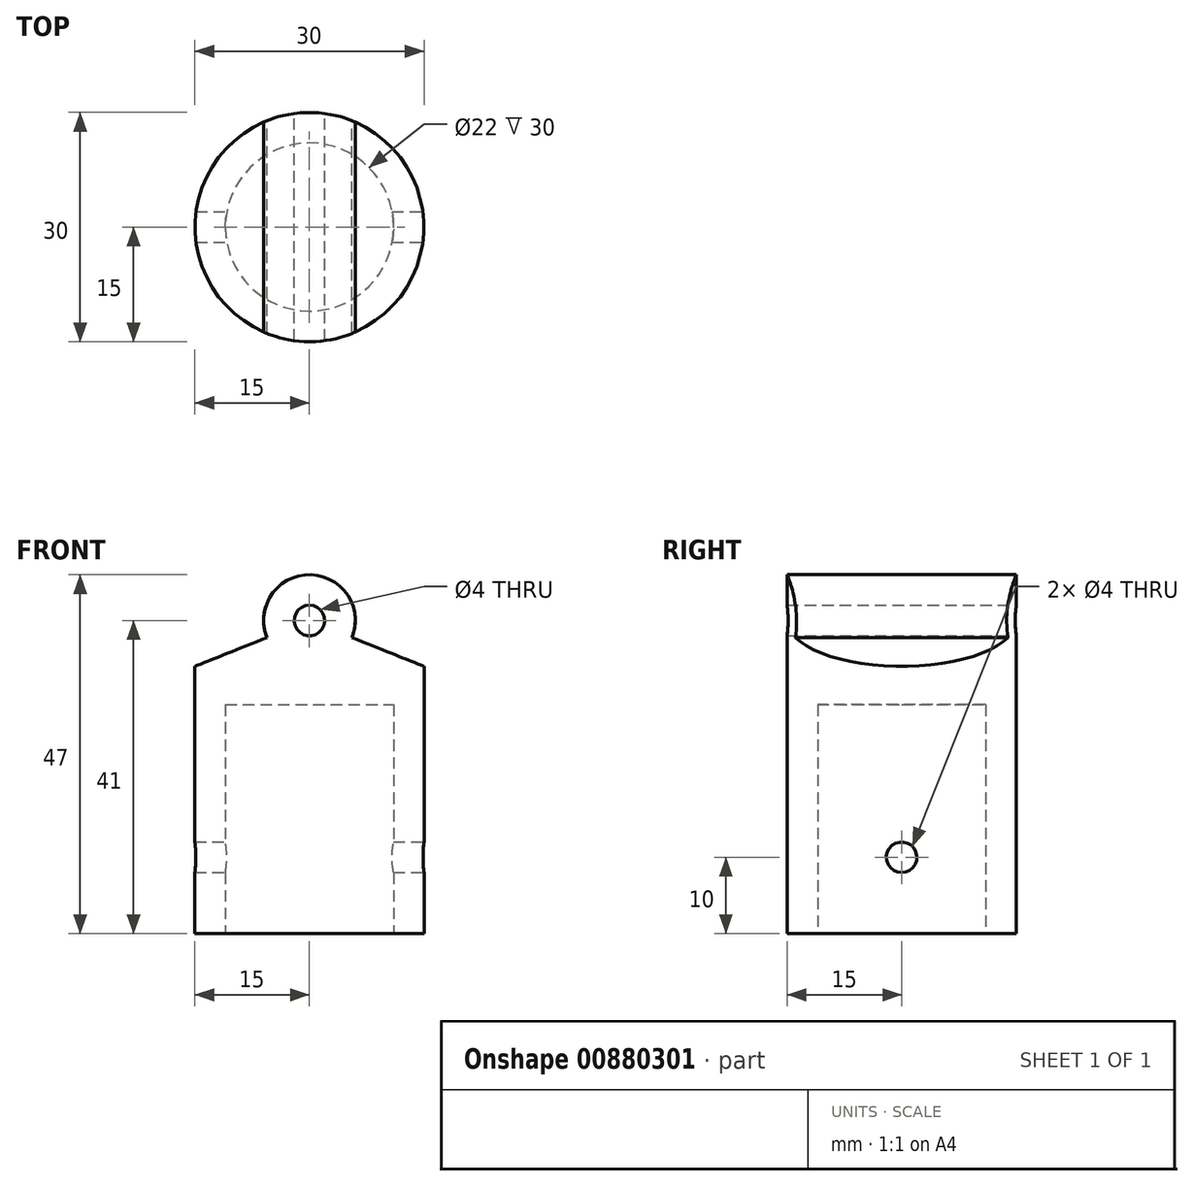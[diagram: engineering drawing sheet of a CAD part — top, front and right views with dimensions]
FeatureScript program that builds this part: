
annotation { "Feature Type Name" : "Feature", "Feature Type Description" : "" }
export const myFeature = defineFeature(function(context is Context, id is Id, definition is map)
    precondition{}
    {
        {
            var Q0;
            Q0=qCreatedBy(makeId("Top.planeOp"),FACE);
            var sketch = newSketch(context, id + "F0", { "sketchPlane" : qUnion([Q0])});
            skCircle(sketch, "E0", {"center": v(0, 0) * mm, "radius": 15 * mm});
            skSolve(sketch);
        }
        {
            var Q0;
            Q0=makeQuery(id+"F0.imprint","IMPRINT",FACE,{"disambiguationData":[TD([[makeQuery(id+"F0.imprint","IMPRINT",EDGE,{"derivedFrom":sQuery(id+"F0.wireOp",EDGE,"E0")}),1.0]])]});
            extrude(context, id + "F1", {"entities" : qUnion([Q0]), "depth" : 35 * mm, "offsetDistance" : 25 * mm});
        }
        {
            var Q0;
            Q0=qCreatedBy(makeId("Front.planeOp"),FACE);
            var sketch = newSketch(context, id + "F2", { "sketchPlane" : qUnion([Q0])});
            skCircle(sketch, "E1", {"center": v(0, 41) * mm, "radius": 6 * mm});
            skCircle(sketch, "E2", {"center": v(0, 41) * mm, "radius": 2 * mm});
            skLineSegment(sketch, "E3", {"start": v(-15, 35) * mm, "end": v(15, 35) * mm});
            skLineSegment(sketch, "E4", {"start": v(-15, 35) * mm, "end": v(0, 41) * mm});
            skLineSegment(sketch, "E5", {"start": v(15, 35) * mm, "end": v(0, 41) * mm});
            skSolve(sketch);
        }
        {
            var Q0;
            {var subQ0=sQuery(id+"F2.wireOp",EDGE,"E3");var subQ1=sQuery(id+"F2.wireOp",EDGE,"E1");var subQ2=makeQuery(id+"F2.imprint","INTERSECT",VERTEX,{"derivedFrom":[subQ1,subQ0]});Q0=makeQuery(id+"F2.imprint","IMPRINT",FACE,{"disambiguationData":[TD([[makeQuery(id+"F2.imprint","IMPRINT",EDGE,{"disambiguationData":[TD([[subQ2,1.0]])],"derivedFrom":subQ1}),-1.0]])]});}
            var Q1;
            {var subQ1=sQuery(id+"F2.wireOp",EDGE,"E1");var subQ7=makeQuery(id+"F2.imprint","INTERSECT",VERTEX,{"derivedFrom":[subQ1,sQuery(id+"F2.wireOp",EDGE,"E3")]});Q1=makeQuery(id+"F2.imprint","IMPRINT",FACE,{"disambiguationData":[TD([[makeQuery(id+"F2.imprint","IMPRINT",EDGE,{"disambiguationData":[TD([[subQ7,1.0]])],"derivedFrom":subQ1}),1.0]])]});}
            var Q2;
            {var subQ0=sQuery(id+"F2.wireOp",EDGE,"E3");var subQ1=sQuery(id+"F2.wireOp",EDGE,"E1");var subQ2=makeQuery(id+"F2.imprint","INTERSECT",VERTEX,{"derivedFrom":[subQ1,subQ0]});Q2=makeQuery(id+"F2.imprint","IMPRINT",FACE,{"disambiguationData":[TD([[makeQuery(id+"F2.imprint","IMPRINT",EDGE,{"disambiguationData":[TD([[subQ2,-1.0]])],"derivedFrom":subQ1}),-1.0]])]});}
            var Q3;
            {var subQ0=sQuery(id+"F2.wireOp",EDGE,"E4");var subQ1=sQuery(id+"F2.wireOp",EDGE,"E1");var subQ2=makeQuery(id+"F2.imprint","INTERSECT",VERTEX,{"derivedFrom":[subQ1,subQ0]});Q3=makeQuery(id+"F2.imprint","IMPRINT",FACE,{"disambiguationData":[TD([[makeQuery(id+"F2.imprint","IMPRINT",EDGE,{"disambiguationData":[TD([[subQ2,1.0]])],"derivedFrom":subQ1}),1.0]])]});}
            extrude(context, id + "F3", {"entities" : qUnion([Q0, Q1, Q2, Q3]), "operationType" : NewBodyOperationType.ADD, "endBound" : BoundingType.SYMMETRIC, "depth" : 30 * mm, "offsetDistance" : 25 * mm});
        }
        {
            var Q0;
            Q0=makeQuery(id+"F1.opExtrude","CAP_FACE",FACE,{"disambiguationData":[OSD([sQuery(id+"F0.wireOp",EDGE,"E0")])],"isStart":true});
            var sketch = newSketch(context, id + "F4", { "sketchPlane" : qUnion([Q0])});
            skLineSegment(sketch, "E6.bottom", {"start": v(-17.1, 17.75) * mm, "end": v(19.31, 17.75) * mm});
            skLineSegment(sketch, "E6.top", {"start": v(-17.1, -18.1) * mm, "end": v(19.31, -18.1) * mm});
            skLineSegment(sketch, "E6.left", {"start": v(-17.1, 17.75) * mm, "end": v(-17.1, -18.1) * mm});
            skLineSegment(sketch, "E6.right", {"start": v(19.31, 17.75) * mm, "end": v(19.31, -18.1) * mm});
            skCircle(sketch, "E7", {"center": v(0, 0) * mm, "radius": 15 * mm});
            skSolve(sketch);
        }
        {
            var Q0;
            Q0=makeQuery(id+"F4.imprint","IMPRINT",FACE,{"disambiguationData":[TD([[makeQuery(id+"F4.imprint","IMPRINT",EDGE,{"derivedFrom":sQuery(id+"F4.wireOp",EDGE,"E6.bottom")}),-1.0]])]});
            extrude(context, id + "F5", {"entities" : qUnion([Q0]), "operationType" : NewBodyOperationType.REMOVE, "oppositeDirection" : true, "depth" : 50 * mm, "offsetDistance" : 25 * mm});
        }
        {
            var Q0;
            Q0=makeQuery(id+"F1.opExtrude","CAP_FACE",FACE,{"disambiguationData":[OSD([sQuery(id+"F0.wireOp",EDGE,"E0")])],"isStart":true});
            var sketch = newSketch(context, id + "F6", { "sketchPlane" : qUnion([Q0])});
            skCircle(sketch, "E8", {"center": v(0, 0) * mm, "radius": 11 * mm});
            skSolve(sketch);
        }
        {
            var Q0;
            Q0=makeQuery(id+"F6.imprint","IMPRINT",FACE,{"disambiguationData":[TD([[makeQuery(id+"F6.imprint","IMPRINT",EDGE,{"derivedFrom":sQuery(id+"F6.wireOp",EDGE,"E8")}),1.0]])]});
            extrude(context, id + "F7", {"entities" : qUnion([Q0]), "operationType" : NewBodyOperationType.REMOVE, "oppositeDirection" : true, "depth" : 30 * mm, "offsetDistance" : 25 * mm});
        }
        {
            var Q0;
            Q0=qCreatedBy(makeId("Right.planeOp"),FACE);
            var sketch = newSketch(context, id + "F8", { "sketchPlane" : qUnion([Q0])});
            skCircle(sketch, "E9", {"center": v(0, 10) * mm, "radius": 2 * mm});
            skSolve(sketch);
        }
        {
            var Q0;
            Q0 = qSketchRegion(id + "F8", true);
            extrude(context, id + "F9", {"entities" : qUnion([Q0]), "operationType" : NewBodyOperationType.REMOVE, "endBound" : BoundingType.SYMMETRIC, "oppositeDirection" : true, "depth" : 30 * mm, "offsetDistance" : 25 * mm});
        }
    });
